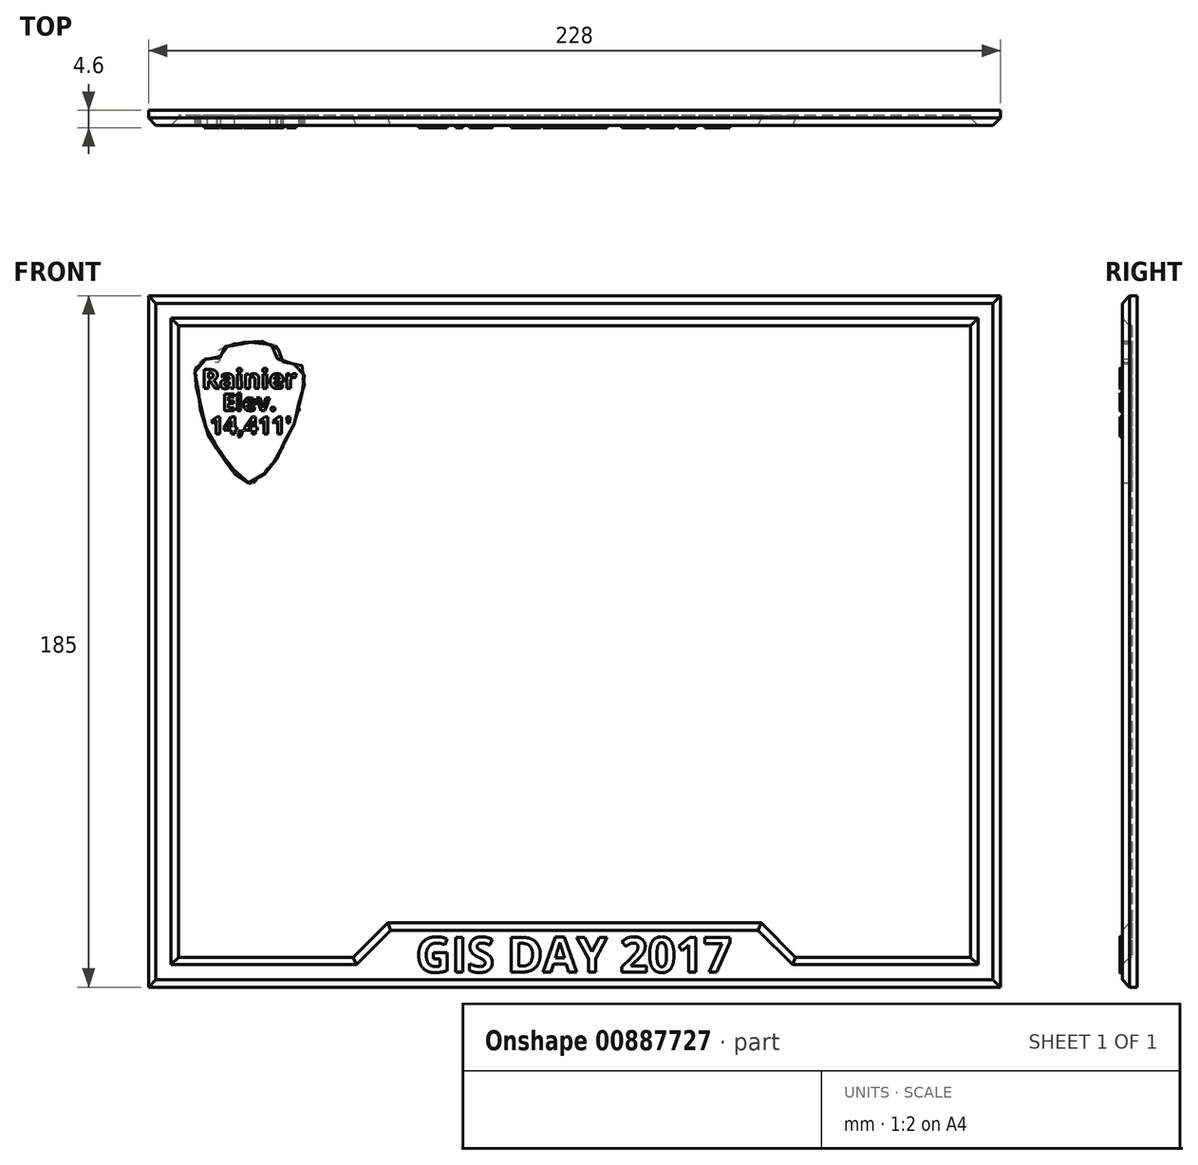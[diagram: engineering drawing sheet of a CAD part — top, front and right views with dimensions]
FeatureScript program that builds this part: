
annotation { "Feature Type Name" : "Feature", "Feature Type Description" : "" }
export const myFeature = defineFeature(function(context is Context, id is Id, definition is map)
    precondition{}
    {
        {
            var Q0;
            Q0=qCreatedBy(makeId("Front.planeOp"),FACE);
            var sketch = newSketch(context, id + "F0", { "sketchPlane" : qUnion([Q0])});
            skLineSegment(sketch, "E0.bottom", {"start": v(114, 92.5) * mm, "end": v(-114, 92.5) * mm});
            skLineSegment(sketch, "E0.top", {"start": v(114, -92.5) * mm, "end": v(-114, -92.5) * mm});
            skLineSegment(sketch, "E0.left", {"start": v(114, 92.5) * mm, "end": v(114, -92.5) * mm});
            skLineSegment(sketch, "E0.right", {"start": v(-114, 92.5) * mm, "end": v(-114, -92.5) * mm});
            skPoint(sketch, "E0.middle", {"position": v(0, 0) * mm});
            skLineSegment(sketch, "E1.0", {"start": v(106, 84.5) * mm, "end": v(-106, 84.5) * mm});
            skLineSegment(sketch, "E1.1", {"start": v(106, 84.5) * mm, "end": v(106, -84.5) * mm});
            skLineSegment(sketch, "E1.2", {"start": v(106, -84.5) * mm, "end": v(59.2, -84.5) * mm});
            skLineSegment(sketch, "E1.3", {"start": v(-106, 84.5) * mm, "end": v(-106, -84.5) * mm});
            skLineSegment(sketch, "E2", {"start": v(0, 0) * mm, "end": v(0, -102.65) * mm, "construction": true});
            skLineSegment(sketch, "E3", {"start": v(0, -75.3) * mm, "end": v(50, -75.3) * mm});
            skLineSegment(sketch, "E4", {"start": v(50, -75.3) * mm, "end": v(59.2, -84.5) * mm});
            skLineSegment(sketch, "E5.MirrorCS", {"start": v(0, -75.3) * mm, "end": v(-50, -75.3) * mm});
            skLineSegment(sketch, "E6.MirrorCS", {"start": v(-50, -75.3) * mm, "end": v(-59.2, -84.5) * mm});
            skLineSegment(sketch, "E7", {"start": v(-59.2, -84.5) * mm, "end": v(-106, -84.5) * mm});
            skText(sketch, "E8", { "text": "GIS DAY 2017", "fontName": "OpenSans-Bold.ttf"});
            skFitSpline(sketch, "E9", {"points": [v(-87.2, 42.43) * mm, v(-88.61, 43.33) * mm, v(-90.54, 44.55) * mm, v(-91.15, 45.3) * mm, v(-91.19, 45.92) * mm, v(-91.94, 46.24) * mm, v(-92.62, 47.18) * mm, v(-92.7, 47.76) * mm, v(-93.37, 48.3) * mm, v(-93.52, 49.06) * mm, v(-94.37, 49.64) * mm, v(-94.76, 50.73) * mm, v(-95.35, 51.54) * mm, v(-95.78, 51.94) * mm, v(-95.82, 52.4) * mm, v(-96.57, 53.18) * mm, v(-96.91, 53.29) * mm, v(-97.6, 54.8) * mm, v(-98.3, 55.98) * mm, v(-98.34, 56.43) * mm, v(-98.76, 57.44) * mm, v(-98.89, 58.53) * mm, v(-99.2, 60.1) * mm, v(-99.67, 61.59) * mm, v(-100.25, 62.38) * mm, v(-100.14, 64.2) * mm, v(-100.26, 65.63) * mm, v(-100.9, 66.53) * mm, v(-100.69, 66.98) * mm, v(-101.24, 68.65) * mm, v(-101.07, 70.02) * mm, v(-101.02, 71.11) * mm, v(-101.56, 71.7) * mm, v(-101.45, 72.97) * mm, v(-101.5, 74.02) * mm, v(-100.44, 74.54) * mm, v(-99.73, 75.23) * mm, v(-98.3, 75.49) * mm, v(-97.2, 74.93) * mm, v(-95.67, 74.61) * mm, v(-94.98, 74.94) * mm, v(-94.98, 76.37) * mm, v(-95.58, 77.16) * mm, v(-95.53, 77.95) * mm, v(-94.61, 78.13) * mm, v(-93.65, 78.67) * mm, v(-92.26, 79.14) * mm, v(-91.04, 79.61) * mm, v(-90.4, 79.6) * mm, v(-87.66, 80.1) * mm, v(-86.16, 80) * mm, v(-85.13, 80.03) * mm, v(-84.15, 80.3) * mm, v(-82.31, 79.59) * mm, v(-80.09, 79.23) * mm, v(-79.39, 78.22) * mm, v(-78.47, 77.03) * mm, v(-79.37, 76.4) * mm, v(-79.35, 75.3) * mm, v(-78.39, 74.9) * mm, v(-77.5, 74.37) * mm, v(-76, 74.36) * mm, v(-75.27, 74.17) * mm, v(-73.73, 74.32) * mm, v(-73.21, 73.87) * mm, v(-72.53, 73.44) * mm, v(-72.53, 72.48) * mm, v(-72.28, 70.83) * mm, v(-72.69, 70.23) * mm, v(-72.71, 69.65) * mm, v(-72.37, 68.84) * mm, v(-72.7, 67.7) * mm, v(-72.87, 66.44) * mm, v(-73, 65.4) * mm, v(-73.06, 64.64) * mm, v(-73.66, 64.04) * mm, v(-73.88, 63.36) * mm, v(-73.75, 62.35) * mm, v(-73.63, 61.7) * mm, v(-73.95, 60.79) * mm, v(-74.16, 59.67) * mm, v(-74.7, 58.94) * mm, v(-75.15, 58.02) * mm, v(-75.32, 57.32) * mm, v(-75.69, 56.82) * mm, v(-75.82, 56) * mm, v(-76.18, 55.92) * mm, v(-76.66, 55.06) * mm, v(-76.74, 54.61) * mm, v(-77.15, 54.2) * mm, v(-77.88, 53.28) * mm, v(-78.12, 52.45) * mm, v(-78.12, 51.79) * mm, v(-78.65, 51.33) * mm, v(-78.72, 50.7) * mm, v(-79.34, 49.94) * mm, v(-79.94, 49.15) * mm, v(-79.73, 48.8) * mm, v(-80.35, 48.12) * mm, v(-81.57, 47.15) * mm, v(-81.6, 46.66) * mm, v(-82.2, 46.21) * mm, v(-82.62, 45.52) * mm, v(-83.03, 44.84) * mm, v(-84.19, 44.1) * mm, v(-85.24, 43.01) * mm, v(-85.92, 42.48) * mm, v(-86.5, 42.41) * mm, v(-87.2, 42.43) * mm]});
            skText(sketch, "E10", { "text": "Rainier", "fontName": "OpenSans-Bold.ttf"});
            skText(sketch, "E11", { "text": "Elev.", "fontName": "OpenSans-Bold.ttf"});
            skText(sketch, "E12", { "text": "14,411\'", "fontName": "OpenSans-Bold.ttf"});
            const initialGuessF0  = {"E8": [-0.04246, -0.0885, 1, 0, 0.00941], "E10": [-0.09969, 0.0677, 1, 0.00158, 0.0051], "E11": [-0.09418, 0.06175, 1, 0, 0.00448], "E12": [-0.09756, 0.05556, 1, 0, 0.00461]};
            skSetInitialGuess(sketch, initialGuessF0);
            skSolve(sketch);
        }
        {
            var Q0;
            Q0=makeQuery(id+"F0.imprint","IMPRINT",FACE,{"disambiguationData":[TD([[makeQuery(id+"F0.imprint","IMPRINT",EDGE,{"derivedFrom":sQuery(id+"F0.wireOp",EDGE,"E0.bottom")}),1.0]])]});
            var Q1;
            Q1=makeQuery(id+"F0.imprint","IMPRINT",FACE,{"disambiguationData":[TD([[makeQuery(id+"F0.imprint","IMPRINT",EDGE,{"derivedFrom":sQuery(id+"F0.wireOp",EDGE,"E1.0")}),1.0]])]});
            var Q2;
            Q2=makeQuery(id+"F0.imprint","IMPRINT",FACE,{"disambiguationData":[TD([[makeQuery(id+"F0.imprint","IMPRINT",EDGE,{"derivedFrom":sQuery(id+"F0.wireOp",EDGE,"E8.sketch_text.stroke-0")}),-1.0]])]});
            var Q3;
            Q3=makeQuery(id+"F0.imprint","IMPRINT",FACE,{"disambiguationData":[TD([[makeQuery(id+"F0.imprint","IMPRINT",EDGE,{"derivedFrom":sQuery(id+"F0.wireOp",EDGE,"E8.sketch_text.stroke-12")}),-1.0]])]});
            var Q4;
            Q4=makeQuery(id+"F0.imprint","IMPRINT",FACE,{"disambiguationData":[TD([[makeQuery(id+"F0.imprint","IMPRINT",EDGE,{"derivedFrom":sQuery(id+"F0.wireOp",EDGE,"E8.sketch_text.stroke-40")}),-1.0]])]});
            var Q5;
            Q5=makeQuery(id+"F0.imprint","IMPRINT",FACE,{"disambiguationData":[TD([[makeQuery(id+"F0.imprint","IMPRINT",EDGE,{"derivedFrom":sQuery(id+"F0.wireOp",EDGE,"E8.sketch_text.stroke-68")}),-1.0]])]});
            var Q6;
            Q6=makeQuery(id+"F0.imprint","IMPRINT",FACE,{"disambiguationData":[TD([[makeQuery(id+"F0.imprint","IMPRINT",EDGE,{"derivedFrom":sQuery(id+"F0.wireOp",EDGE,"E8.sketch_text.stroke-68")}),1.0]])]});
            var Q7;
            Q7=makeQuery(id+"F0.imprint","IMPRINT",FACE,{"disambiguationData":[TD([[makeQuery(id+"F0.imprint","IMPRINT",EDGE,{"derivedFrom":sQuery(id+"F0.wireOp",EDGE,"E8.sketch_text.stroke-86")}),-1.0]])]});
            var Q8;
            Q8=makeQuery(id+"F0.imprint","IMPRINT",FACE,{"disambiguationData":[TD([[makeQuery(id+"F0.imprint","IMPRINT",EDGE,{"derivedFrom":sQuery(id+"F0.wireOp",EDGE,"E8.sketch_text.stroke-103")}),-1.0]])]});
            var Q9;
            Q9=makeQuery(id+"F0.imprint","IMPRINT",FACE,{"disambiguationData":[TD([[makeQuery(id+"F0.imprint","IMPRINT",EDGE,{"derivedFrom":sQuery(id+"F0.wireOp",EDGE,"E8.sketch_text.stroke-129")}),-1.0]])]});
            var Q10;
            Q10=makeQuery(id+"F0.imprint","IMPRINT",FACE,{"disambiguationData":[TD([[makeQuery(id+"F0.imprint","IMPRINT",EDGE,{"derivedFrom":sQuery(id+"F0.wireOp",EDGE,"E8.sketch_text.stroke-129")}),1.0]])]});
            var Q11;
            Q11=makeQuery(id+"F0.imprint","IMPRINT",FACE,{"disambiguationData":[TD([[makeQuery(id+"F0.imprint","IMPRINT",EDGE,{"derivedFrom":sQuery(id+"F0.wireOp",EDGE,"E8.sketch_text.stroke-148")}),-1.0]])]});
            var Q12;
            Q12=makeQuery(id+"F0.imprint","IMPRINT",FACE,{"disambiguationData":[TD([[makeQuery(id+"F0.imprint","IMPRINT",EDGE,{"derivedFrom":sQuery(id+"F0.wireOp",EDGE,"E8.sketch_text.stroke-148")}),1.0]])]});
            var Q13;
            Q13=makeQuery(id+"F0.imprint","IMPRINT",FACE,{"disambiguationData":[TD([[makeQuery(id+"F0.imprint","IMPRINT",EDGE,{"derivedFrom":sQuery(id+"F0.wireOp",EDGE,"E8.sketch_text.stroke-166")}),-1.0]])]});
            var Q14;
            Q14=makeQuery(id+"F0.imprint","IMPRINT",FACE,{"disambiguationData":[TD([[makeQuery(id+"F0.imprint","IMPRINT",EDGE,{"derivedFrom":sQuery(id+"F0.wireOp",EDGE,"E8.sketch_text.stroke-183")}),-1.0]])]});
            var Q15;
            Q15=makeQuery(id+"F0.imprint","IMPRINT",FACE,{"disambiguationData":[TD([[makeQuery(id+"F0.imprint","IMPRINT",EDGE,{"derivedFrom":sQuery(id+"F0.wireOp",EDGE,"E8.sketch_text.stroke-201")}),-1.0]])]});
            var Q16;
            Q16=makeQuery(id+"F0.imprint","IMPRINT",FACE,{"disambiguationData":[TD([[makeQuery(id+"F0.imprint","IMPRINT",EDGE,{"derivedFrom":sQuery(id+"F0.wireOp",EDGE,"E8.sketch_text.stroke-201")}),1.0]])]});
            var Q17;
            Q17=makeQuery(id+"F0.imprint","IMPRINT",FACE,{"disambiguationData":[TD([[makeQuery(id+"F0.imprint","IMPRINT",EDGE,{"derivedFrom":sQuery(id+"F0.wireOp",EDGE,"E8.sketch_text.stroke-221")}),-1.0]])]});
            var Q18;
            Q18=makeQuery(id+"F0.imprint","IMPRINT",FACE,{"disambiguationData":[TD([[makeQuery(id+"F0.imprint","IMPRINT",EDGE,{"derivedFrom":sQuery(id+"F0.wireOp",EDGE,"E8.sketch_text.stroke-238")}),1.0]])]});
            var Q19;
            Q19=makeQuery(id+"F0.imprint","IMPRINT",FACE,{"disambiguationData":[TD([[makeQuery(id+"F0.imprint","IMPRINT",EDGE,{"derivedFrom":sQuery(id+"F0.wireOp",EDGE,"E8.sketch_text.stroke-246")}),-1.0]])]});
            var Q20;
            Q20=makeQuery(id+"F0.imprint","IMPRINT",FACE,{"disambiguationData":[TD([[makeQuery(id+"F0.imprint","IMPRINT",EDGE,{"derivedFrom":sQuery(id+"F0.wireOp",EDGE,"E8.sketch_text.stroke-250")}),-1.0]])]});
            var Q21;
            Q21=makeQuery(id+"F0.imprint","IMPRINT",FACE,{"disambiguationData":[TD([[makeQuery(id+"F0.imprint","IMPRINT",EDGE,{"derivedFrom":sQuery(id+"F0.wireOp",EDGE,"E8.sketch_text.stroke-260")}),-1.0]])]});
            var Q22;
            Q22=makeQuery(id+"F0.imprint","IMPRINT",FACE,{"disambiguationData":[TD([[makeQuery(id+"F0.imprint","IMPRINT",EDGE,{"derivedFrom":sQuery(id+"F0.wireOp",EDGE,"E8.sketch_text.stroke-284")}),-1.0]])]});
            var Q23;
            Q23=makeQuery(id+"F0.imprint","IMPRINT",FACE,{"disambiguationData":[TD([[makeQuery(id+"F0.imprint","IMPRINT",EDGE,{"derivedFrom":sQuery(id+"F0.wireOp",EDGE,"E8.sketch_text.stroke-288")}),-1.0]])]});
            var Q24;
            Q24=makeQuery(id+"F0.imprint","IMPRINT",FACE,{"disambiguationData":[TD([[makeQuery(id+"F0.imprint","IMPRINT",EDGE,{"derivedFrom":sQuery(id+"F0.wireOp",EDGE,"E8.sketch_text.stroke-298")}),-1.0]])]});
            var Q25;
            Q25=makeQuery(id+"F0.imprint","IMPRINT",FACE,{"disambiguationData":[TD([[makeQuery(id+"F0.imprint","IMPRINT",EDGE,{"derivedFrom":sQuery(id+"F0.wireOp",EDGE,"E9")}),-1.0]])]});
            var Q26;
            Q26=makeQuery(id+"F0.imprint","IMPRINT",FACE,{"disambiguationData":[TD([[makeQuery(id+"F0.imprint","IMPRINT",EDGE,{"derivedFrom":sQuery(id+"F0.wireOp",EDGE,"E10.sketch_text.stroke-99")}),-1.0]])]});
            var Q27;
            Q27=makeQuery(id+"F0.imprint","IMPRINT",FACE,{"disambiguationData":[TD([[makeQuery(id+"F0.imprint","IMPRINT",EDGE,{"derivedFrom":sQuery(id+"F0.wireOp",EDGE,"E10.sketch_text.stroke-79")}),-1.0]])]});
            var Q28;
            Q28=makeQuery(id+"F0.imprint","IMPRINT",FACE,{"disambiguationData":[TD([[makeQuery(id+"F0.imprint","IMPRINT",EDGE,{"derivedFrom":sQuery(id+"F0.wireOp",EDGE,"E10.sketch_text.stroke-79")}),1.0]])]});
            var Q29;
            Q29=makeQuery(id+"F0.imprint","IMPRINT",FACE,{"disambiguationData":[TD([[makeQuery(id+"F0.imprint","IMPRINT",EDGE,{"derivedFrom":sQuery(id+"F0.wireOp",EDGE,"E10.sketch_text.stroke-75")}),-1.0]])]});
            var Q30;
            Q30=makeQuery(id+"F0.imprint","IMPRINT",FACE,{"disambiguationData":[TD([[makeQuery(id+"F0.imprint","IMPRINT",EDGE,{"derivedFrom":sQuery(id+"F0.wireOp",EDGE,"E10.sketch_text.stroke-70")}),-1.0]])]});
            var Q31;
            Q31=makeQuery(id+"F0.imprint","IMPRINT",FACE,{"disambiguationData":[TD([[makeQuery(id+"F0.imprint","IMPRINT",EDGE,{"derivedFrom":sQuery(id+"F0.wireOp",EDGE,"E10.sketch_text.stroke-53")}),-1.0]])]});
            var Q32;
            Q32=makeQuery(id+"F0.imprint","IMPRINT",FACE,{"disambiguationData":[TD([[makeQuery(id+"F0.imprint","IMPRINT",EDGE,{"derivedFrom":sQuery(id+"F0.wireOp",EDGE,"E10.sketch_text.stroke-44")}),-1.0]])]});
            var Q33;
            Q33=makeQuery(id+"F0.imprint","IMPRINT",FACE,{"disambiguationData":[TD([[makeQuery(id+"F0.imprint","IMPRINT",EDGE,{"derivedFrom":sQuery(id+"F0.wireOp",EDGE,"E10.sketch_text.stroke-49")}),-1.0]])]});
            var Q34;
            Q34=makeQuery(id+"F0.imprint","IMPRINT",FACE,{"disambiguationData":[TD([[makeQuery(id+"F0.imprint","IMPRINT",EDGE,{"derivedFrom":sQuery(id+"F0.wireOp",EDGE,"E10.sketch_text.stroke-19")}),-1.0]])]});
            var Q35;
            Q35=makeQuery(id+"F0.imprint","IMPRINT",FACE,{"disambiguationData":[TD([[makeQuery(id+"F0.imprint","IMPRINT",EDGE,{"derivedFrom":sQuery(id+"F0.wireOp",EDGE,"E10.sketch_text.stroke-37")}),1.0]])]});
            var Q36;
            Q36=makeQuery(id+"F0.imprint","IMPRINT",FACE,{"disambiguationData":[TD([[makeQuery(id+"F0.imprint","IMPRINT",EDGE,{"derivedFrom":sQuery(id+"F0.wireOp",EDGE,"E10.sketch_text.stroke-0")}),-1.0]])]});
            var Q37;
            Q37=makeQuery(id+"F0.imprint","IMPRINT",FACE,{"disambiguationData":[TD([[makeQuery(id+"F0.imprint","IMPRINT",EDGE,{"derivedFrom":sQuery(id+"F0.wireOp",EDGE,"E10.sketch_text.stroke-0")}),1.0]])]});
            var Q38;
            Q38=makeQuery(id+"F0.imprint","IMPRINT",FACE,{"disambiguationData":[TD([[makeQuery(id+"F0.imprint","IMPRINT",EDGE,{"derivedFrom":sQuery(id+"F0.wireOp",EDGE,"E11.sketch_text.stroke-0")}),-1.0]])]});
            var Q39;
            Q39=makeQuery(id+"F0.imprint","IMPRINT",FACE,{"disambiguationData":[TD([[makeQuery(id+"F0.imprint","IMPRINT",EDGE,{"derivedFrom":sQuery(id+"F0.wireOp",EDGE,"E11.sketch_text.stroke-12")}),-1.0]])]});
            var Q40;
            Q40=makeQuery(id+"F0.imprint","IMPRINT",FACE,{"disambiguationData":[TD([[makeQuery(id+"F0.imprint","IMPRINT",EDGE,{"derivedFrom":sQuery(id+"F0.wireOp",EDGE,"E11.sketch_text.stroke-16")}),-1.0]])]});
            var Q41;
            Q41=makeQuery(id+"F0.imprint","IMPRINT",FACE,{"disambiguationData":[TD([[makeQuery(id+"F0.imprint","IMPRINT",EDGE,{"derivedFrom":sQuery(id+"F0.wireOp",EDGE,"E11.sketch_text.stroke-16")}),1.0]])]});
            var Q42;
            Q42=makeQuery(id+"F0.imprint","IMPRINT",FACE,{"disambiguationData":[TD([[makeQuery(id+"F0.imprint","IMPRINT",EDGE,{"derivedFrom":sQuery(id+"F0.wireOp",EDGE,"E11.sketch_text.stroke-36")}),-1.0]])]});
            var Q43;
            Q43=makeQuery(id+"F0.imprint","IMPRINT",FACE,{"disambiguationData":[TD([[makeQuery(id+"F0.imprint","IMPRINT",EDGE,{"derivedFrom":sQuery(id+"F0.wireOp",EDGE,"E11.sketch_text.stroke-46")}),-1.0]])]});
            var Q44;
            Q44=makeQuery(id+"F0.imprint","IMPRINT",FACE,{"disambiguationData":[TD([[makeQuery(id+"F0.imprint","IMPRINT",EDGE,{"derivedFrom":sQuery(id+"F0.wireOp",EDGE,"E12.sketch_text.stroke-0")}),-1.0]])]});
            var Q45;
            Q45=makeQuery(id+"F0.imprint","IMPRINT",FACE,{"disambiguationData":[TD([[makeQuery(id+"F0.imprint","IMPRINT",EDGE,{"derivedFrom":sQuery(id+"F0.wireOp",EDGE,"E12.sketch_text.stroke-10")}),-1.0]])]});
            var Q46;
            Q46=makeQuery(id+"F0.imprint","IMPRINT",FACE,{"disambiguationData":[TD([[makeQuery(id+"F0.imprint","IMPRINT",EDGE,{"derivedFrom":sQuery(id+"F0.wireOp",EDGE,"E12.sketch_text.stroke-21")}),1.0]])]});
            var Q47;
            Q47=makeQuery(id+"F0.imprint","IMPRINT",FACE,{"disambiguationData":[TD([[makeQuery(id+"F0.imprint","IMPRINT",EDGE,{"derivedFrom":sQuery(id+"F0.wireOp",EDGE,"E12.sketch_text.stroke-28")}),-1.0]])]});
            var Q48;
            Q48=makeQuery(id+"F0.imprint","IMPRINT",FACE,{"disambiguationData":[TD([[makeQuery(id+"F0.imprint","IMPRINT",EDGE,{"derivedFrom":sQuery(id+"F0.wireOp",EDGE,"E12.sketch_text.stroke-33")}),-1.0]])]});
            var Q49;
            Q49=makeQuery(id+"F0.imprint","IMPRINT",FACE,{"disambiguationData":[TD([[makeQuery(id+"F0.imprint","IMPRINT",EDGE,{"derivedFrom":sQuery(id+"F0.wireOp",EDGE,"E12.sketch_text.stroke-44")}),1.0]])]});
            var Q50;
            Q50=makeQuery(id+"F0.imprint","IMPRINT",FACE,{"disambiguationData":[TD([[makeQuery(id+"F0.imprint","IMPRINT",EDGE,{"derivedFrom":sQuery(id+"F0.wireOp",EDGE,"E12.sketch_text.stroke-51")}),-1.0]])]});
            var Q51;
            Q51=makeQuery(id+"F0.imprint","IMPRINT",FACE,{"disambiguationData":[TD([[makeQuery(id+"F0.imprint","IMPRINT",EDGE,{"derivedFrom":sQuery(id+"F0.wireOp",EDGE,"E12.sketch_text.stroke-61")}),-1.0]])]});
            var Q52;
            Q52=makeQuery(id+"F0.imprint","IMPRINT",FACE,{"disambiguationData":[TD([[makeQuery(id+"F0.imprint","IMPRINT",EDGE,{"derivedFrom":sQuery(id+"F0.wireOp",EDGE,"E12.sketch_text.stroke-69")}),1.0]])]});
            var Q53;
            Q53=makeQuery(id+"F0.imprint","IMPRINT",FACE,{"disambiguationData":[TD([[makeQuery(id+"F0.imprint","IMPRINT",EDGE,{"derivedFrom":sQuery(id+"F0.wireOp",EDGE,"E12.sketch_text.stroke-77")}),-1.0]])]});
            var Q54;
            Q54=makeQuery(id+"F0.imprint","IMPRINT",FACE,{"disambiguationData":[TD([[makeQuery(id+"F0.imprint","IMPRINT",EDGE,{"derivedFrom":sQuery(id+"F0.wireOp",EDGE,"E8.sketch_text.stroke-58")}),1.0]])]});
            var Q55;
            Q55=makeQuery(id+"F0.imprint","IMPRINT",FACE,{"disambiguationData":[TD([[makeQuery(id+"F0.imprint","IMPRINT",EDGE,{"derivedFrom":sQuery(id+"F0.wireOp",EDGE,"E8.sketch_text.stroke-19")}),-1.0]])]});
            var Q56;
            Q56=makeQuery(id+"F0.imprint","IMPRINT",FACE,{"disambiguationData":[TD([[makeQuery(id+"F0.imprint","IMPRINT",EDGE,{"derivedFrom":sQuery(id+"F0.wireOp",EDGE,"E8.sketch_text.stroke-51")}),-1.0]])]});
            var Q57;
            Q57=makeQuery(id+"F0.imprint","IMPRINT",FACE,{"disambiguationData":[TD([[makeQuery(id+"F0.imprint","IMPRINT",EDGE,{"derivedFrom":sQuery(id+"F0.wireOp",EDGE,"E8.sketch_text.stroke-81")}),1.0]])]});
            var Q58;
            Q58=makeQuery(id+"F0.imprint","IMPRINT",FACE,{"disambiguationData":[TD([[makeQuery(id+"F0.imprint","IMPRINT",EDGE,{"derivedFrom":sQuery(id+"F0.wireOp",EDGE,"E8.sketch_text.stroke-105")}),-1.0]])]});
            var Q59;
            Q59=makeQuery(id+"F0.imprint","IMPRINT",FACE,{"disambiguationData":[TD([[makeQuery(id+"F0.imprint","IMPRINT",EDGE,{"derivedFrom":sQuery(id+"F0.wireOp",EDGE,"E8.sketch_text.stroke-137")}),1.0]])]});
            var Q60;
            Q60=makeQuery(id+"F0.imprint","IMPRINT",FACE,{"disambiguationData":[TD([[makeQuery(id+"F0.imprint","IMPRINT",EDGE,{"derivedFrom":sQuery(id+"F0.wireOp",EDGE,"E8.sketch_text.stroke-178")}),1.0]])]});
            var Q61;
            Q61=makeQuery(id+"F0.imprint","IMPRINT",FACE,{"disambiguationData":[TD([[makeQuery(id+"F0.imprint","IMPRINT",EDGE,{"derivedFrom":sQuery(id+"F0.wireOp",EDGE,"E8.sketch_text.stroke-171")}),1.0]])]});
            var Q62;
            Q62=makeQuery(id+"F0.imprint","IMPRINT",FACE,{"disambiguationData":[TD([[makeQuery(id+"F0.imprint","IMPRINT",EDGE,{"derivedFrom":sQuery(id+"F0.wireOp",EDGE,"E8.sketch_text.stroke-71")}),1.0]])]});
            var Q63;
            Q63=makeQuery(id+"F0.imprint","IMPRINT",FACE,{"disambiguationData":[TD([[makeQuery(id+"F0.imprint","IMPRINT",EDGE,{"derivedFrom":sQuery(id+"F0.wireOp",EDGE,"E8.sketch_text.stroke-75")}),-1.0]])]});
            var Q64;
            Q64=makeQuery(id+"F0.imprint","IMPRINT",FACE,{"disambiguationData":[TD([[makeQuery(id+"F0.imprint","IMPRINT",EDGE,{"derivedFrom":sQuery(id+"F0.wireOp",EDGE,"E8.sketch_text.stroke-108")}),-1.0]])]});
            var Q65;
            Q65=makeQuery(id+"F0.imprint","IMPRINT",FACE,{"disambiguationData":[TD([[makeQuery(id+"F0.imprint","IMPRINT",EDGE,{"derivedFrom":sQuery(id+"F0.wireOp",EDGE,"E8.sketch_text.stroke-116")}),1.0]])]});
            var Q66;
            Q66=makeQuery(id+"F0.imprint","IMPRINT",FACE,{"disambiguationData":[TD([[makeQuery(id+"F0.imprint","IMPRINT",EDGE,{"derivedFrom":sQuery(id+"F0.wireOp",EDGE,"E8.sketch_text.stroke-157")}),1.0]])]});
            var Q67;
            Q67=makeQuery(id+"F0.imprint","IMPRINT",FACE,{"disambiguationData":[TD([[makeQuery(id+"F0.imprint","IMPRINT",EDGE,{"derivedFrom":sQuery(id+"F0.wireOp",EDGE,"E8.sketch_text.stroke-150")}),1.0]])]});
            var Q68;
            Q68=makeQuery(id+"F0.imprint","IMPRINT",FACE,{"disambiguationData":[TD([[makeQuery(id+"F0.imprint","IMPRINT",EDGE,{"derivedFrom":sQuery(id+"F0.wireOp",EDGE,"E12.sketch_text.stroke-71")}),-1.0]])]});
            var Q69;
            Q69=makeQuery(id+"F0.imprint","IMPRINT",FACE,{"disambiguationData":[TD([[makeQuery(id+"F0.imprint","IMPRINT",EDGE,{"derivedFrom":sQuery(id+"F0.wireOp",EDGE,"E8.sketch_text.stroke-134")}),-1.0]])]});
            extrude(context, id + "F1", {"entities" : qUnion([Q0, Q1, Q2, Q3, Q4, Q5, Q6, Q7, Q8, Q9, Q10, Q11, Q12, Q13, Q14, Q15, Q16, Q17, Q18, Q19, Q20, Q21, Q22, Q23, Q24, Q25, Q26, Q27, Q28, Q29, Q30, Q31, Q32, Q33, Q34, Q35, Q36, Q37, Q38, Q39, Q40, Q41, Q42, Q43, Q44, Q45, Q46, Q47, Q48, Q49, Q50, Q51, Q52, Q53, Q54, Q55, Q56, Q57, Q58, Q59, Q60, Q61, Q62, Q63, Q64, Q65, Q66, Q67, Q68, Q69]), "oppositeDirection" : true, "depth" : 4 * mm, "offsetDistance" : 25 * mm});
        }
        {
            var Q0;
            Q0=makeQuery(id+"F0.imprint","IMPRINT",FACE,{"disambiguationData":[TD([[makeQuery(id+"F0.imprint","IMPRINT",EDGE,{"derivedFrom":sQuery(id+"F0.wireOp",EDGE,"E1.0")}),1.0]])]});
            extrude(context, id + "F2", {"entities" : qUnion([Q0]), "operationType" : NewBodyOperationType.REMOVE, "oppositeDirection" : true, "depth" : 2.6 * mm, "offsetDistance" : 25 * mm});
        }
        {
            var Q0;
            Q0=makeQuery(id+"F1.opExtrude","CAP_EDGE",EDGE,{"disambiguationData":[OSD([sQuery(id+"F0.wireOp",EDGE,"E0.left")])],"isStart":true});
            var Q1;
            Q1=makeQuery(id+"F1.opExtrude","CAP_EDGE",EDGE,{"disambiguationData":[OSD([sQuery(id+"F0.wireOp",EDGE,"E0.top")])],"isStart":true});
            var Q2;
            Q2=makeQuery(id+"F1.opExtrude","CAP_EDGE",EDGE,{"disambiguationData":[OSD([sQuery(id+"F0.wireOp",EDGE,"E0.right")])],"isStart":true});
            var Q3;
            Q3=makeQuery(id+"F1.opExtrude","CAP_EDGE",EDGE,{"disambiguationData":[OSD([sQuery(id+"F0.wireOp",EDGE,"E0.bottom")])],"isStart":true});
            var Q4;
            Q4=makeQuery(id+"F2.boolean.opBoolean","COPY",EDGE,{"derivedFrom":makeQuery(id+"F2.opExtrude","CAP_EDGE",EDGE,{"disambiguationData":[OSD([sQuery(id+"F0.wireOp",EDGE,"E1.0")])],"isStart":true})});
            var Q5;
            Q5=makeQuery(id+"F2.boolean.opBoolean","COPY",EDGE,{"derivedFrom":makeQuery(id+"F2.opExtrude","CAP_EDGE",EDGE,{"disambiguationData":[OSD([sQuery(id+"F0.wireOp",EDGE,"E1.3")])],"isStart":true})});
            var Q6;
            Q6=makeQuery(id+"F2.boolean.opBoolean","COPY",EDGE,{"derivedFrom":makeQuery(id+"F2.opExtrude","CAP_EDGE",EDGE,{"disambiguationData":[OSD([sQuery(id+"F0.wireOp",EDGE,"E1.1")])],"isStart":true})});
            var Q7;
            Q7=makeQuery(id+"F2.boolean.opBoolean","COPY",EDGE,{"derivedFrom":makeQuery(id+"F2.opExtrude","CAP_EDGE",EDGE,{"disambiguationData":[OSD([sQuery(id+"F0.wireOp",EDGE,"E1.2")])],"isStart":true})});
            var Q8;
            Q8=makeQuery(id+"F2.boolean.opBoolean","COPY",EDGE,{"derivedFrom":makeQuery(id+"F2.opExtrude","CAP_EDGE",EDGE,{"disambiguationData":[OSD([sQuery(id+"F0.wireOp",EDGE,"E7")])],"isStart":true})});
            var Q9;
            Q9=makeQuery(id+"F2.boolean.opBoolean","COPY",EDGE,{"derivedFrom":makeQuery(id+"F2.opExtrude","CAP_EDGE",EDGE,{"disambiguationData":[OSD([sQuery(id+"F0.wireOp",EDGE,"E6.MirrorCS")])],"isStart":true})});
            var Q10;
            Q10=makeQuery(id+"F2.boolean.opBoolean","COPY",EDGE,{"derivedFrom":makeQuery(id+"F2.opExtrude","CAP_EDGE",EDGE,{"disambiguationData":[OSD([sQuery(id+"F0.wireOp",EDGE,"E3"),sQuery(id+"F0.wireOp",EDGE,"E5.MirrorCS")])],"isStart":true})});
            var Q11;
            Q11=makeQuery(id+"F2.boolean.opBoolean","COPY",EDGE,{"derivedFrom":makeQuery(id+"F2.opExtrude","CAP_EDGE",EDGE,{"disambiguationData":[OSD([sQuery(id+"F0.wireOp",EDGE,"E4")])],"isStart":true})});
            chamfer(context, id + "F3", {"entities" : qUnion([Q0, Q1, Q2, Q3, Q4, Q5, Q6, Q7, Q8, Q9, Q10, Q11]), "width" : 2 * mm, "tangentPropagation" : true});
        }
        {
            var Q0;
            Q0=makeQuery(id+"F0.imprint","IMPRINT",FACE,{"disambiguationData":[TD([[makeQuery(id+"F0.imprint","IMPRINT",EDGE,{"derivedFrom":sQuery(id+"F0.wireOp",EDGE,"E12.sketch_text.stroke-33")}),-1.0]])]});
            var Q1;
            Q1=makeQuery(id+"F0.imprint","IMPRINT",FACE,{"disambiguationData":[TD([[makeQuery(id+"F0.imprint","IMPRINT",EDGE,{"derivedFrom":sQuery(id+"F0.wireOp",EDGE,"E12.sketch_text.stroke-51")}),-1.0]])]});
            var Q2;
            Q2=makeQuery(id+"F0.imprint","IMPRINT",FACE,{"disambiguationData":[TD([[makeQuery(id+"F0.imprint","IMPRINT",EDGE,{"derivedFrom":sQuery(id+"F0.wireOp",EDGE,"E12.sketch_text.stroke-61")}),-1.0]])]});
            var Q3;
            Q3=makeQuery(id+"F0.imprint","IMPRINT",FACE,{"disambiguationData":[TD([[makeQuery(id+"F0.imprint","IMPRINT",EDGE,{"derivedFrom":sQuery(id+"F0.wireOp",EDGE,"E12.sketch_text.stroke-77")}),-1.0]])]});
            var Q4;
            Q4=makeQuery(id+"F0.imprint","IMPRINT",FACE,{"disambiguationData":[TD([[makeQuery(id+"F0.imprint","IMPRINT",EDGE,{"derivedFrom":sQuery(id+"F0.wireOp",EDGE,"E12.sketch_text.stroke-28")}),-1.0]])]});
            var Q5;
            Q5=makeQuery(id+"F0.imprint","IMPRINT",FACE,{"disambiguationData":[TD([[makeQuery(id+"F0.imprint","IMPRINT",EDGE,{"derivedFrom":sQuery(id+"F0.wireOp",EDGE,"E12.sketch_text.stroke-10")}),-1.0]])]});
            var Q6;
            Q6=makeQuery(id+"F0.imprint","IMPRINT",FACE,{"disambiguationData":[TD([[makeQuery(id+"F0.imprint","IMPRINT",EDGE,{"derivedFrom":sQuery(id+"F0.wireOp",EDGE,"E12.sketch_text.stroke-0")}),-1.0]])]});
            var Q7;
            Q7=makeQuery(id+"F0.imprint","IMPRINT",FACE,{"disambiguationData":[TD([[makeQuery(id+"F0.imprint","IMPRINT",EDGE,{"derivedFrom":sQuery(id+"F0.wireOp",EDGE,"E11.sketch_text.stroke-46")}),-1.0]])]});
            var Q8;
            Q8=makeQuery(id+"F0.imprint","IMPRINT",FACE,{"disambiguationData":[TD([[makeQuery(id+"F0.imprint","IMPRINT",EDGE,{"derivedFrom":sQuery(id+"F0.wireOp",EDGE,"E11.sketch_text.stroke-36")}),-1.0]])]});
            var Q9;
            Q9=makeQuery(id+"F0.imprint","IMPRINT",FACE,{"disambiguationData":[TD([[makeQuery(id+"F0.imprint","IMPRINT",EDGE,{"derivedFrom":sQuery(id+"F0.wireOp",EDGE,"E11.sketch_text.stroke-16")}),-1.0]])]});
            var Q10;
            Q10=makeQuery(id+"F0.imprint","IMPRINT",FACE,{"disambiguationData":[TD([[makeQuery(id+"F0.imprint","IMPRINT",EDGE,{"derivedFrom":sQuery(id+"F0.wireOp",EDGE,"E11.sketch_text.stroke-12")}),-1.0]])]});
            var Q11;
            Q11=makeQuery(id+"F0.imprint","IMPRINT",FACE,{"disambiguationData":[TD([[makeQuery(id+"F0.imprint","IMPRINT",EDGE,{"derivedFrom":sQuery(id+"F0.wireOp",EDGE,"E11.sketch_text.stroke-0")}),-1.0]])]});
            var Q12;
            Q12=makeQuery(id+"F0.imprint","IMPRINT",FACE,{"disambiguationData":[TD([[makeQuery(id+"F0.imprint","IMPRINT",EDGE,{"derivedFrom":sQuery(id+"F0.wireOp",EDGE,"E10.sketch_text.stroke-99")}),-1.0]])]});
            var Q13;
            Q13=makeQuery(id+"F0.imprint","IMPRINT",FACE,{"disambiguationData":[TD([[makeQuery(id+"F0.imprint","IMPRINT",EDGE,{"derivedFrom":sQuery(id+"F0.wireOp",EDGE,"E10.sketch_text.stroke-79")}),-1.0]])]});
            var Q14;
            Q14=makeQuery(id+"F0.imprint","IMPRINT",FACE,{"disambiguationData":[TD([[makeQuery(id+"F0.imprint","IMPRINT",EDGE,{"derivedFrom":sQuery(id+"F0.wireOp",EDGE,"E10.sketch_text.stroke-75")}),-1.0]])]});
            var Q15;
            Q15=makeQuery(id+"F0.imprint","IMPRINT",FACE,{"disambiguationData":[TD([[makeQuery(id+"F0.imprint","IMPRINT",EDGE,{"derivedFrom":sQuery(id+"F0.wireOp",EDGE,"E10.sketch_text.stroke-70")}),-1.0]])]});
            var Q16;
            Q16=makeQuery(id+"F0.imprint","IMPRINT",FACE,{"disambiguationData":[TD([[makeQuery(id+"F0.imprint","IMPRINT",EDGE,{"derivedFrom":sQuery(id+"F0.wireOp",EDGE,"E10.sketch_text.stroke-53")}),-1.0]])]});
            var Q17;
            Q17=makeQuery(id+"F0.imprint","IMPRINT",FACE,{"disambiguationData":[TD([[makeQuery(id+"F0.imprint","IMPRINT",EDGE,{"derivedFrom":sQuery(id+"F0.wireOp",EDGE,"E10.sketch_text.stroke-44")}),-1.0]])]});
            var Q18;
            Q18=makeQuery(id+"F0.imprint","IMPRINT",FACE,{"disambiguationData":[TD([[makeQuery(id+"F0.imprint","IMPRINT",EDGE,{"derivedFrom":sQuery(id+"F0.wireOp",EDGE,"E10.sketch_text.stroke-49")}),-1.0]])]});
            var Q19;
            Q19=makeQuery(id+"F0.imprint","IMPRINT",FACE,{"disambiguationData":[TD([[makeQuery(id+"F0.imprint","IMPRINT",EDGE,{"derivedFrom":sQuery(id+"F0.wireOp",EDGE,"E10.sketch_text.stroke-19")}),-1.0]])]});
            var Q20;
            Q20=makeQuery(id+"F0.imprint","IMPRINT",FACE,{"disambiguationData":[TD([[makeQuery(id+"F0.imprint","IMPRINT",EDGE,{"derivedFrom":sQuery(id+"F0.wireOp",EDGE,"E10.sketch_text.stroke-0")}),-1.0]])]});
            var Q21;
            Q21=makeQuery(id+"F0.imprint","IMPRINT",FACE,{"disambiguationData":[TD([[makeQuery(id+"F0.imprint","IMPRINT",EDGE,{"derivedFrom":sQuery(id+"F0.wireOp",EDGE,"E8.sketch_text.stroke-0")}),-1.0]])]});
            var Q22;
            Q22=makeQuery(id+"F0.imprint","IMPRINT",FACE,{"disambiguationData":[TD([[makeQuery(id+"F0.imprint","IMPRINT",EDGE,{"derivedFrom":sQuery(id+"F0.wireOp",EDGE,"E8.sketch_text.stroke-12")}),-1.0]])]});
            var Q23;
            Q23=makeQuery(id+"F0.imprint","IMPRINT",FACE,{"disambiguationData":[TD([[makeQuery(id+"F0.imprint","IMPRINT",EDGE,{"derivedFrom":sQuery(id+"F0.wireOp",EDGE,"E8.sketch_text.stroke-40")}),-1.0]])]});
            var Q24;
            Q24=makeQuery(id+"F0.imprint","IMPRINT",FACE,{"disambiguationData":[TD([[makeQuery(id+"F0.imprint","IMPRINT",EDGE,{"derivedFrom":sQuery(id+"F0.wireOp",EDGE,"E8.sketch_text.stroke-68")}),-1.0]])]});
            var Q25;
            Q25=makeQuery(id+"F0.imprint","IMPRINT",FACE,{"disambiguationData":[TD([[makeQuery(id+"F0.imprint","IMPRINT",EDGE,{"derivedFrom":sQuery(id+"F0.wireOp",EDGE,"E8.sketch_text.stroke-86")}),-1.0]])]});
            var Q26;
            Q26=makeQuery(id+"F0.imprint","IMPRINT",FACE,{"disambiguationData":[TD([[makeQuery(id+"F0.imprint","IMPRINT",EDGE,{"derivedFrom":sQuery(id+"F0.wireOp",EDGE,"E8.sketch_text.stroke-103")}),-1.0]])]});
            var Q27;
            Q27=makeQuery(id+"F0.imprint","IMPRINT",FACE,{"disambiguationData":[TD([[makeQuery(id+"F0.imprint","IMPRINT",EDGE,{"derivedFrom":sQuery(id+"F0.wireOp",EDGE,"E8.sketch_text.stroke-129")}),-1.0]])]});
            var Q28;
            Q28=makeQuery(id+"F0.imprint","IMPRINT",FACE,{"disambiguationData":[TD([[makeQuery(id+"F0.imprint","IMPRINT",EDGE,{"derivedFrom":sQuery(id+"F0.wireOp",EDGE,"E8.sketch_text.stroke-148")}),-1.0]])]});
            var Q29;
            Q29=makeQuery(id+"F0.imprint","IMPRINT",FACE,{"disambiguationData":[TD([[makeQuery(id+"F0.imprint","IMPRINT",EDGE,{"derivedFrom":sQuery(id+"F0.wireOp",EDGE,"E8.sketch_text.stroke-166")}),-1.0]])]});
            var Q30;
            Q30=makeQuery(id+"F0.imprint","IMPRINT",FACE,{"disambiguationData":[TD([[makeQuery(id+"F0.imprint","IMPRINT",EDGE,{"derivedFrom":sQuery(id+"F0.wireOp",EDGE,"E8.sketch_text.stroke-183")}),-1.0]])]});
            var Q31;
            Q31=makeQuery(id+"F0.imprint","IMPRINT",FACE,{"disambiguationData":[TD([[makeQuery(id+"F0.imprint","IMPRINT",EDGE,{"derivedFrom":sQuery(id+"F0.wireOp",EDGE,"E8.sketch_text.stroke-201")}),-1.0]])]});
            var Q32;
            Q32=makeQuery(id+"F0.imprint","IMPRINT",FACE,{"disambiguationData":[TD([[makeQuery(id+"F0.imprint","IMPRINT",EDGE,{"derivedFrom":sQuery(id+"F0.wireOp",EDGE,"E8.sketch_text.stroke-221")}),-1.0]])]});
            var Q33;
            Q33=makeQuery(id+"F0.imprint","IMPRINT",FACE,{"disambiguationData":[TD([[makeQuery(id+"F0.imprint","IMPRINT",EDGE,{"derivedFrom":sQuery(id+"F0.wireOp",EDGE,"E8.sketch_text.stroke-246")}),-1.0]])]});
            var Q34;
            Q34=makeQuery(id+"F0.imprint","IMPRINT",FACE,{"disambiguationData":[TD([[makeQuery(id+"F0.imprint","IMPRINT",EDGE,{"derivedFrom":sQuery(id+"F0.wireOp",EDGE,"E8.sketch_text.stroke-250")}),-1.0]])]});
            var Q35;
            Q35=makeQuery(id+"F0.imprint","IMPRINT",FACE,{"disambiguationData":[TD([[makeQuery(id+"F0.imprint","IMPRINT",EDGE,{"derivedFrom":sQuery(id+"F0.wireOp",EDGE,"E8.sketch_text.stroke-260")}),-1.0]])]});
            var Q36;
            Q36=makeQuery(id+"F0.imprint","IMPRINT",FACE,{"disambiguationData":[TD([[makeQuery(id+"F0.imprint","IMPRINT",EDGE,{"derivedFrom":sQuery(id+"F0.wireOp",EDGE,"E8.sketch_text.stroke-284")}),-1.0]])]});
            var Q37;
            Q37=makeQuery(id+"F0.imprint","IMPRINT",FACE,{"disambiguationData":[TD([[makeQuery(id+"F0.imprint","IMPRINT",EDGE,{"derivedFrom":sQuery(id+"F0.wireOp",EDGE,"E8.sketch_text.stroke-288")}),-1.0]])]});
            var Q38;
            Q38=makeQuery(id+"F0.imprint","IMPRINT",FACE,{"disambiguationData":[TD([[makeQuery(id+"F0.imprint","IMPRINT",EDGE,{"derivedFrom":sQuery(id+"F0.wireOp",EDGE,"E8.sketch_text.stroke-298")}),-1.0]])]});
            var Q39;
            Q39=makeQuery(id+"F0.imprint","IMPRINT",FACE,{"disambiguationData":[TD([[makeQuery(id+"F0.imprint","IMPRINT",EDGE,{"derivedFrom":sQuery(id+"F0.wireOp",EDGE,"E8.sketch_text.stroke-19")}),-1.0]])]});
            var Q40;
            Q40=makeQuery(id+"F0.imprint","IMPRINT",FACE,{"disambiguationData":[TD([[makeQuery(id+"F0.imprint","IMPRINT",EDGE,{"derivedFrom":sQuery(id+"F0.wireOp",EDGE,"E8.sketch_text.stroke-51")}),-1.0]])]});
            var Q41;
            Q41=makeQuery(id+"F0.imprint","IMPRINT",FACE,{"disambiguationData":[TD([[makeQuery(id+"F0.imprint","IMPRINT",EDGE,{"derivedFrom":sQuery(id+"F0.wireOp",EDGE,"E8.sketch_text.stroke-105")}),-1.0]])]});
            var Q42;
            Q42=makeQuery(id+"F0.imprint","IMPRINT",FACE,{"disambiguationData":[TD([[makeQuery(id+"F0.imprint","IMPRINT",EDGE,{"derivedFrom":sQuery(id+"F0.wireOp",EDGE,"E8.sketch_text.stroke-75")}),-1.0]])]});
            var Q43;
            Q43=makeQuery(id+"F0.imprint","IMPRINT",FACE,{"disambiguationData":[TD([[makeQuery(id+"F0.imprint","IMPRINT",EDGE,{"derivedFrom":sQuery(id+"F0.wireOp",EDGE,"E8.sketch_text.stroke-108")}),-1.0]])]});
            var Q44;
            Q44=makeQuery(id+"F0.imprint","IMPRINT",FACE,{"disambiguationData":[TD([[makeQuery(id+"F0.imprint","IMPRINT",EDGE,{"derivedFrom":sQuery(id+"F0.wireOp",EDGE,"E12.sketch_text.stroke-71")}),-1.0]])]});
            var Q45;
            Q45=makeQuery(id+"F0.imprint","IMPRINT",FACE,{"disambiguationData":[TD([[makeQuery(id+"F0.imprint","IMPRINT",EDGE,{"derivedFrom":sQuery(id+"F0.wireOp",EDGE,"E8.sketch_text.stroke-134")}),-1.0]])]});
            extrude(context, id + "F4", {"entities" : qUnion([Q0, Q1, Q2, Q3, Q4, Q5, Q6, Q7, Q8, Q9, Q10, Q11, Q12, Q13, Q14, Q15, Q16, Q17, Q18, Q19, Q20, Q21, Q22, Q23, Q24, Q25, Q26, Q27, Q28, Q29, Q30, Q31, Q32, Q33, Q34, Q35, Q36, Q37, Q38, Q39, Q40, Q41, Q42, Q43, Q44, Q45]), "operationType" : NewBodyOperationType.ADD, "depth" : 0.6 * mm, "offsetDistance" : 25 * mm});
        }
        {
            var Q0;
            Q0=makeQuery(id+"F2.boolean.opBoolean","COPY",EDGE,{"derivedFrom":makeQuery(id+"F2.opExtrude","CAP_EDGE",EDGE,{"disambiguationData":[OSD([sQuery(id+"F0.wireOp",EDGE,"E9")])],"isStart":true})});
            var Q1;
            Q1=makeQuery(id+"F2.boolean.opBoolean","COPY",EDGE,{"derivedFrom":makeQuery(id+"F2.opExtrude","CAP_EDGE",EDGE,{"disambiguationData":[OSD([sQuery(id+"F0.wireOp",EDGE,"E9")])],"isStart":false})});
            chamfer(context, id + "F5", {"entities" : qUnion([Q0, Q1]), "width" : .1 * mm});
        }
    });
